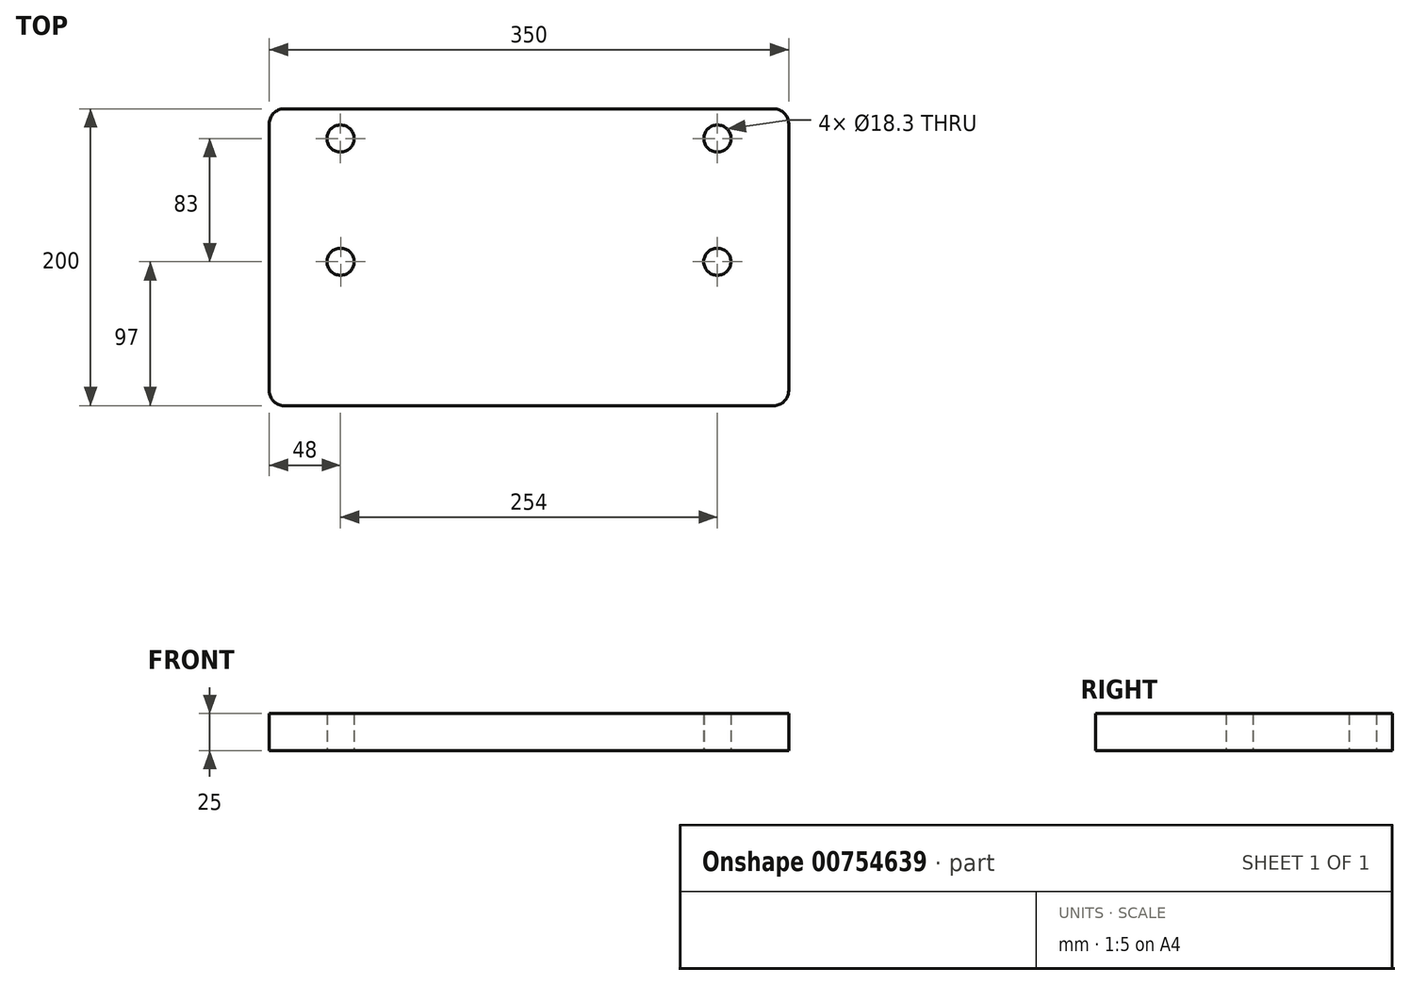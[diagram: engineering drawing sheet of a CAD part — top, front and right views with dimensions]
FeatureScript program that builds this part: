
annotation { "Feature Type Name" : "Feature", "Feature Type Description" : "" }
export const myFeature = defineFeature(function(context is Context, id is Id, definition is map)
    precondition{}
    {
        {
            var Q0;
            Q0=qCreatedBy(makeId("Top.planeOp"),FACE);
            var sketch = newSketch(context, id + "F0", { "sketchPlane" : qUnion([Q0])});
            skLineSegment(sketch, "E0.top", {"start": v(0, 200) * mm, "end": v(350, 200) * mm});
            skLineSegment(sketch, "E0.left", {"start": v(0, 0) * mm, "end": v(0, 200) * mm});
            skLineSegment(sketch, "E0.right", {"start": v(350, 0) * mm, "end": v(350, 200) * mm});
            skLineSegment(sketch, "E1", {"start": v(0, 0) * mm, "end": v(350, 0) * mm});
            skPoint(sketch, "E2.end.orphan", {"position": v(175, 0) * mm});
            skPoint(sketch, "E2.start.orphan", {"position": v(175, 200) * mm});
            skLineSegment(sketch, "E3", {"start": v(175, 200) * mm, "end": v(175, 180) * mm});
            skCircle(sketch, "E4", {"center": v(48, 180) * mm, "radius": 9.15 * mm});
            skCircle(sketch, "E5", {"center": v(48.06, 97) * mm, "radius": 9.15 * mm});
            skCircle(sketch, "E6.MirrorC", {"center": v(302, 180) * mm, "radius": 9.15 * mm});
            skCircle(sketch, "E7.MirrorC", {"center": v(301.94, 97) * mm, "radius": 9.15 * mm});
            skSolve(sketch);
        }
        {
            var Q0;
            {var subQ1=sQuery(id+"F0.wireOp",EDGE,"E0.left");Q0=makeQuery(id+"F0.imprint","IMPRINT",FACE,{"disambiguationData":[TD([[makeQuery(id+"F0.imprint","IMPRINT",EDGE,{"derivedFrom":subQ1}),-1.0]])]});}
            extrude(context, id + "F1", {"entities" : qUnion([Q0]), "depth" : 25 * mm, "offsetDistance" : 25 * mm});
        }
        {
            var Q0;
            Q0=makeQuery(id+"F1.opExtrude","SWEPT_EDGE",EDGE,{"disambiguationData":[OSD([sQuery(id+"F0.wireOp",EDGE,"E0.right"),sQuery(id+"F0.wireOp",EDGE,"E1")])]});
            var Q1;
            Q1=makeQuery(id+"F1.opExtrude","SWEPT_EDGE",EDGE,{"disambiguationData":[OSD([sQuery(id+"F0.wireOp",EDGE,"E0.top"),sQuery(id+"F0.wireOp",EDGE,"E0.right")])]});
            var Q2;
            Q2=makeQuery(id+"F1.opExtrude","SWEPT_EDGE",EDGE,{"disambiguationData":[OSD([sQuery(id+"F0.wireOp",EDGE,"E0.left"),sQuery(id+"F0.wireOp",EDGE,"E1")])]});
            var Q3;
            Q3=makeQuery(id+"F1.opExtrude","SWEPT_EDGE",EDGE,{"disambiguationData":[OSD([sQuery(id+"F0.wireOp",EDGE,"E0.top"),sQuery(id+"F0.wireOp",EDGE,"E0.left")])]});
            fillet(context, id + "F2", {"entities" : qUnion([Q0, Q1, Q2, Q3]), "radius" : 10 * mm, "tangentPropagation" : true, "allowEdgeOverflow" : false});
        }
    });
